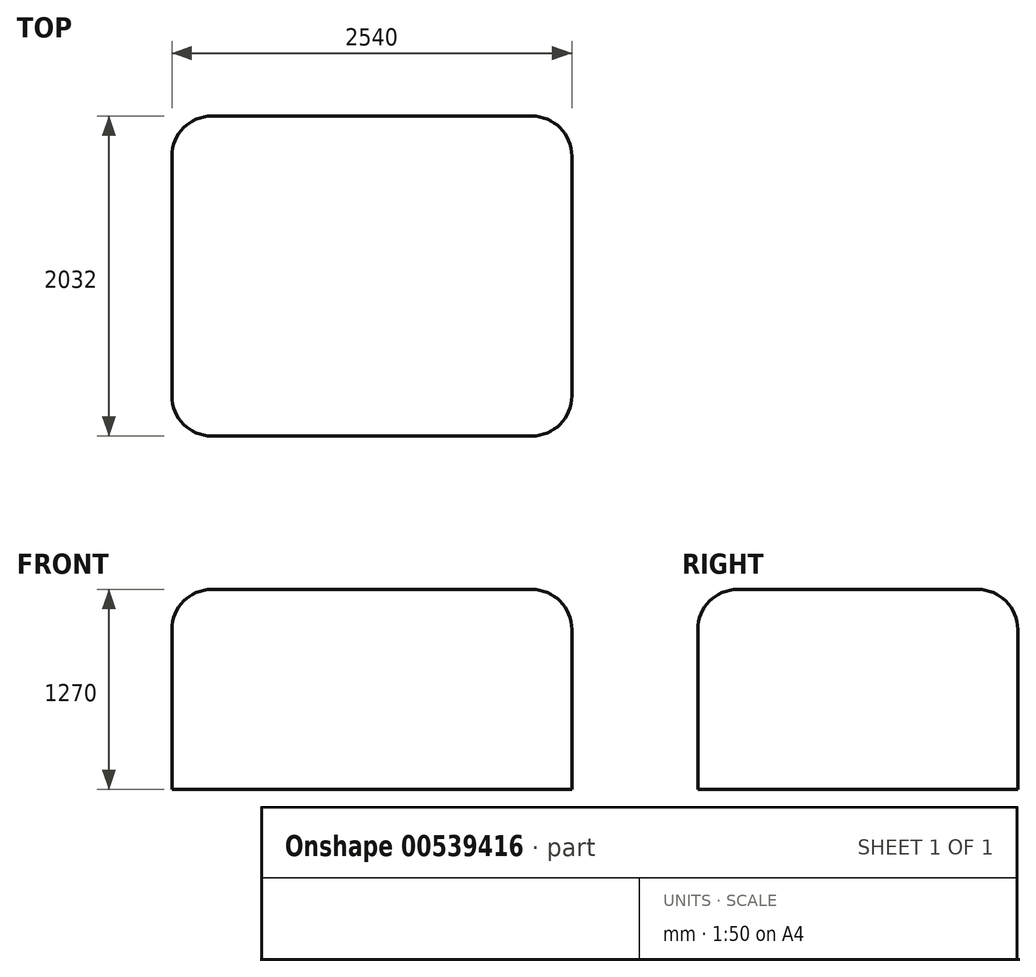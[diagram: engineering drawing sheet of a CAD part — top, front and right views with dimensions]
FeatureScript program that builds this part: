
annotation { "Feature Type Name" : "Feature", "Feature Type Description" : "" }
export const myFeature = defineFeature(function(context is Context, id is Id, definition is map)
    precondition{}
    {
        {
            var Q0;
            Q0=qCreatedBy(makeId("Top.planeOp"),FACE);
            var sketch = newSketch(context, id + "F0", { "sketchPlane" : qUnion([Q0])});
            skLineSegment(sketch, "E0.bottom", {"start": v(-1270, 1016) * mm, "end": v(1270, 1016) * mm});
            skLineSegment(sketch, "E0.top", {"start": v(-1270, -1016) * mm, "end": v(1270, -1016) * mm});
            skLineSegment(sketch, "E0.left", {"start": v(-1270, 1016) * mm, "end": v(-1270, -1016) * mm});
            skLineSegment(sketch, "E0.right", {"start": v(1270, 1016) * mm, "end": v(1270, -1016) * mm});
            skSolve(sketch);
        }
        {
            var Q0;
            Q0 = qSketchRegion(id + "F0", true);
            extrude(context, id + "F1", {"entities" : qUnion([Q0]), "depth" : 1270 * mm, "offsetDistance" : 25.4 * mm});
        }
        {
            var Q0;
            Q0=makeQuery(id+"F1.opExtrude","CAP_EDGE",EDGE,{"disambiguationData":[OSD([sQuery(id+"F0.wireOp",EDGE,"E0.bottom")])],"isStart":false});
            var Q1;
            Q1=makeQuery(id+"F1.opExtrude","CAP_EDGE",EDGE,{"disambiguationData":[OSD([sQuery(id+"F0.wireOp",EDGE,"E0.left")])],"isStart":false});
            var Q2;
            Q2=makeQuery(id+"F1.opExtrude","CAP_EDGE",EDGE,{"disambiguationData":[OSD([sQuery(id+"F0.wireOp",EDGE,"E0.top")])],"isStart":false});
            var Q3;
            Q3=makeQuery(id+"F1.opExtrude","CAP_EDGE",EDGE,{"disambiguationData":[OSD([sQuery(id+"F0.wireOp",EDGE,"E0.right")])],"isStart":false});
            var Q4;
            Q4=makeQuery(id+"F1.opExtrude","SWEPT_EDGE",EDGE,{"disambiguationData":[OSD([sQuery(id+"F0.wireOp",EDGE,"E0.top"),sQuery(id+"F0.wireOp",EDGE,"E0.left")])]});
            var Q5;
            Q5=makeQuery(id+"F1.opExtrude","SWEPT_EDGE",EDGE,{"disambiguationData":[OSD([sQuery(id+"F0.wireOp",EDGE,"E0.bottom"),sQuery(id+"F0.wireOp",EDGE,"E0.left")])]});
            var Q6;
            Q6=makeQuery(id+"F1.opExtrude","SWEPT_EDGE",EDGE,{"disambiguationData":[OSD([sQuery(id+"F0.wireOp",EDGE,"E0.bottom"),sQuery(id+"F0.wireOp",EDGE,"E0.right")])]});
            var Q7;
            Q7=makeQuery(id+"F1.opExtrude","SWEPT_EDGE",EDGE,{"disambiguationData":[OSD([sQuery(id+"F0.wireOp",EDGE,"E0.top"),sQuery(id+"F0.wireOp",EDGE,"E0.right")])]});
            fillet(context, id + "F2", {"entities" : qUnion([Q0, Q1, Q2, Q3, Q4, Q5, Q6, Q7]), "radius" : 254 * mm, "tangentPropagation" : true, "allowEdgeOverflow" : false});
        }
    });
